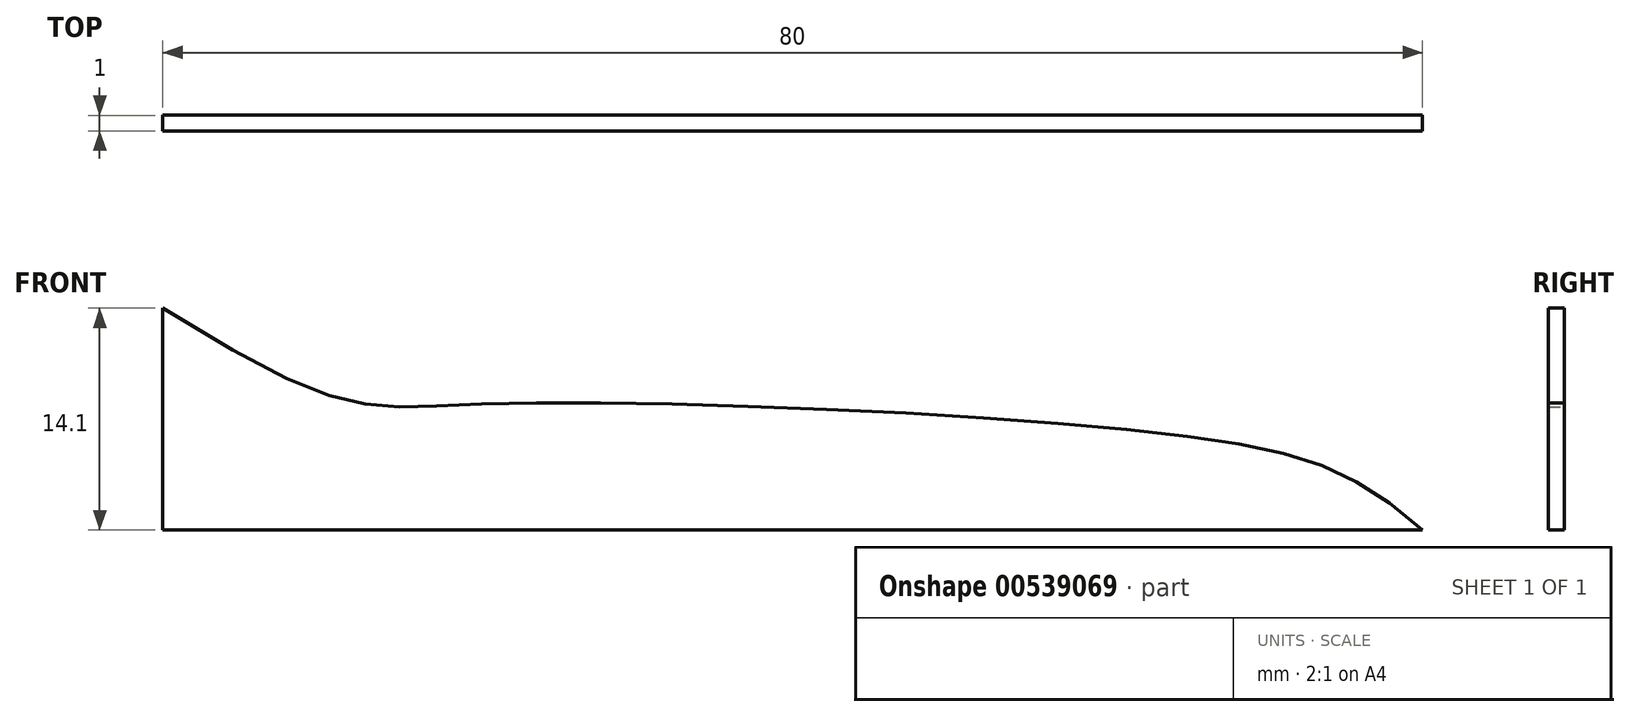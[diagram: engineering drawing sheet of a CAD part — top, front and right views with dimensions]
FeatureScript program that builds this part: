
annotation { "Feature Type Name" : "Feature", "Feature Type Description" : "" }
export const myFeature = defineFeature(function(context is Context, id is Id, definition is map)
    precondition{}
    {
        {
            var Q0;
            Q0=qCreatedBy(makeId("Front.planeOp"),FACE);
            var sketch = newSketch(context, id + "F0", { "sketchPlane" : qUnion([Q0])});
            skLineSegment(sketch, "E0.bottom", {"start": v(0, 0) * mm, "end": v(80, 0) * mm});
            skLineSegment(sketch, "E0.top", {"start": v(0, 15) * mm, "end": v(80, 15) * mm});
            skLineSegment(sketch, "E0.left", {"start": v(0, 0) * mm, "end": v(0, 15) * mm});
            skLineSegment(sketch, "E0.right", {"start": v(80, 0) * mm, "end": v(80, 15) * mm});
            skSolve(sketch);
        }
        {
            var Q0;
            Q0=makeQuery(id+"F0.imprint","IMPRINT",FACE,{"disambiguationData":[TD([[makeQuery(id+"F0.imprint","IMPRINT",EDGE,{"derivedFrom":sQuery(id+"F0.wireOp",EDGE,"E0.bottom")}),1.0]])]});
            extrude(context, id + "F1", {"entities" : qUnion([Q0]), "oppositeDirection" : true, "depth" : 10 * mm, "offsetDistance" : 25 * mm});
        }
        {
            var Q0;
            Q0=makeQuery(id+"F1.opExtrude","SWEPT_FACE",FACE,{"disambiguationData":[OSD([sQuery(id+"F0.wireOp",EDGE,"E0.right")])]});
            var sketch = newSketch(context, id + "F2", { "sketchPlane" : qUnion([Q0])});
            skLineSegment(sketch, "E1", {"start": v(3.86, 0) * mm, "end": v(3.86, 14.1) * mm});
            skLineSegment(sketch, "E2", {"start": v(3.86, 14.1) * mm, "end": v(4.86, 14.1) * mm});
            skLineSegment(sketch, "E3", {"start": v(4.86, 14.1) * mm, "end": v(4.86, 0) * mm});
            skSolve(sketch);
        }
        {
            var Q0;
            {var subQ2=sQuery(id+"F2.wireOp",EDGE,"OKCZ274E-hILO-mRBT-RGVA-Bd56LceW8CBx");Q0=makeQuery(id+"F2.imprint","IMPRINT",FACE,{"disambiguationData":[TD([[makeQuery(id+"F2.imprint","IMPRINT",EDGE,{"derivedFrom":subQ2}),1.0]])]});}
            var Q1;
            {var subQ2=sQuery(id+"F2.wireOp",EDGE,"E1");Q1=makeQuery(id+"F2.imprint","IMPRINT",FACE,{"disambiguationData":[TD([[makeQuery(id+"F2.imprint","IMPRINT",EDGE,{"derivedFrom":subQ2}),1.0]])]});}
            extrude(context, id + "F3", {"entities" : qUnion([Q0, Q1]), "operationType" : NewBodyOperationType.REMOVE, "endBound" : BoundingType.UP_TO_NEXT, "oppositeDirection" : true, "depth" : 35 * mm, "offsetDistance" : 25 * mm});
        }
        {
            var Q0;
            Q0=makeQuery(id+"F3.boolean.opBoolean","COPY",FACE,{"derivedFrom":makeQuery(id+"F3.opExtrude","SWEPT_FACE",FACE,{"disambiguationData":[OSD([sQuery(id+"F2.wireOp",EDGE,"E1")])]})});
            var sketch = newSketch(context, id + "F4", { "sketchPlane" : qUnion([Q0])});
            skFitSpline(sketch, "E4", {"points": [v(0, 14.1) * mm, v(19.67, 8) * mm, v(64.78, 6) * mm, v(80, 0) * mm], "startDerivative": vector(115.83, -72.47) * mm, "endDerivative": vector(49.27, -44.7) * mm});
            skSolve(sketch);
        }
        {
            var Q0;
            Q0=makeQuery(id+"F4.imprint","IMPRINT",FACE,{"disambiguationData":[TD([[makeQuery(id+"F4.imprint","IMPRINT",EDGE,{"derivedFrom":sQuery(id+"F4.wireOp",EDGE,"E4")}),1.0]])]});
            extrude(context, id + "F5", {"entities" : qUnion([Q0]), "operationType" : NewBodyOperationType.REMOVE, "endBound" : BoundingType.UP_TO_NEXT, "oppositeDirection" : true, "depth" : 25 * mm, "offsetDistance" : 25 * mm});
        }
    });
